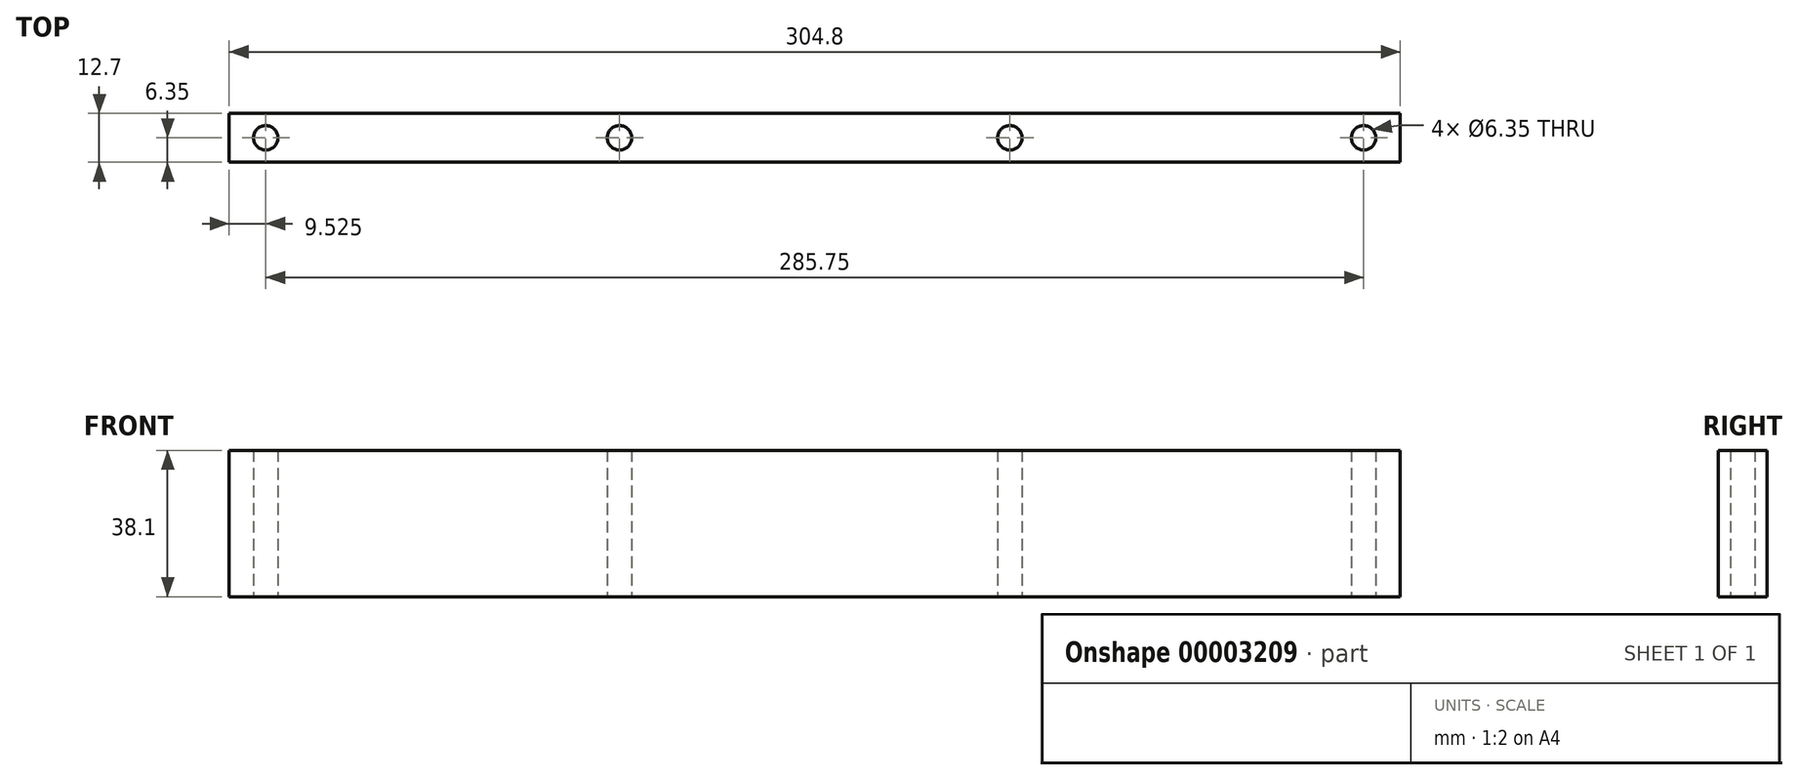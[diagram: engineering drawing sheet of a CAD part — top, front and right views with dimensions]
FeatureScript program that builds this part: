
annotation { "Feature Type Name" : "Feature", "Feature Type Description" : "" }
export const myFeature = defineFeature(function(context is Context, id is Id, definition is map)
    precondition{}
    {
        {
            var Q0;
            Q0=qCreatedBy(makeId("Front.planeOp"),FACE);
            var sketch = newSketch(context, id + "F0", { "sketchPlane" : qUnion([Q0])});
            skLineSegment(sketch, "E0", {"start": v(0, 0) * mm, "end": v(0, -38.1) * mm});
            skLineSegment(sketch, "E1", {"start": v(0, -38.1) * mm, "end": v(304.8, -38.1) * mm});
            skLineSegment(sketch, "E2", {"start": v(304.8, -38.1) * mm, "end": v(304.8, 0) * mm});
            skLineSegment(sketch, "E3", {"start": v(304.8, 0) * mm, "end": v(0, 0) * mm});
            skSolve(sketch);
        }
        {
            var Q0;
            Q0 = qSketchRegion(id + "F0", true);
            extrude(context, id + "F1", {"entities" : qUnion([Q0]), "endBound" : BoundingType.SYMMETRIC, "depth" : 12.7 * mm});
        }
        {
            var Q0;
            Q0=makeQuery(id+"F1.opExtrude","SWEPT_FACE",FACE,{"disambiguationData":[OSD([sQuery(id+"F0.wireOp",EDGE,"E1")])]});
            var sketch = newSketch(context, id + "F2", { "sketchPlane" : qUnion([Q0])});
            skLineSegment(sketch, "E4", {"start": v(0, 0) * mm, "end": v(304.8, 0) * mm, "construction": true});
            skLineSegment(sketch, "E5", {"start": v(9.53, 6.35) * mm, "end": v(9.53, -6.35) * mm, "construction": true});
            skLineSegment(sketch, "E6", {"start": v(101.6, 6.35) * mm, "end": v(101.6, -6.35) * mm, "construction": true});
            skLineSegment(sketch, "E7", {"start": v(203.2, 6.35) * mm, "end": v(203.2, -6.35) * mm, "construction": true});
            skLineSegment(sketch, "E8", {"start": v(295.28, 6.35) * mm, "end": v(295.28, -6.35) * mm, "construction": true});
            skCircle(sketch, "E9", {"center": v(9.53, 0) * mm, "radius": 3.18 * mm});
            skCircle(sketch, "E10", {"center": v(101.6, 0) * mm, "radius": 3.18 * mm});
            skCircle(sketch, "E11", {"center": v(203.2, 0) * mm, "radius": 3.18 * mm});
            skCircle(sketch, "E12", {"center": v(295.28, 0) * mm, "radius": 3.18 * mm});
            skSolve(sketch);
        }
        {
            var Q0;
            Q0 = qSketchRegion(id + "F2", true);
            extrude(context, id + "F3", {"entities" : qUnion([Q0]), "operationType" : NewBodyOperationType.REMOVE, "endBound" : BoundingType.THROUGH_ALL, "oppositeDirection" : true, "depth" : 25.4 * mm});
        }
    });
